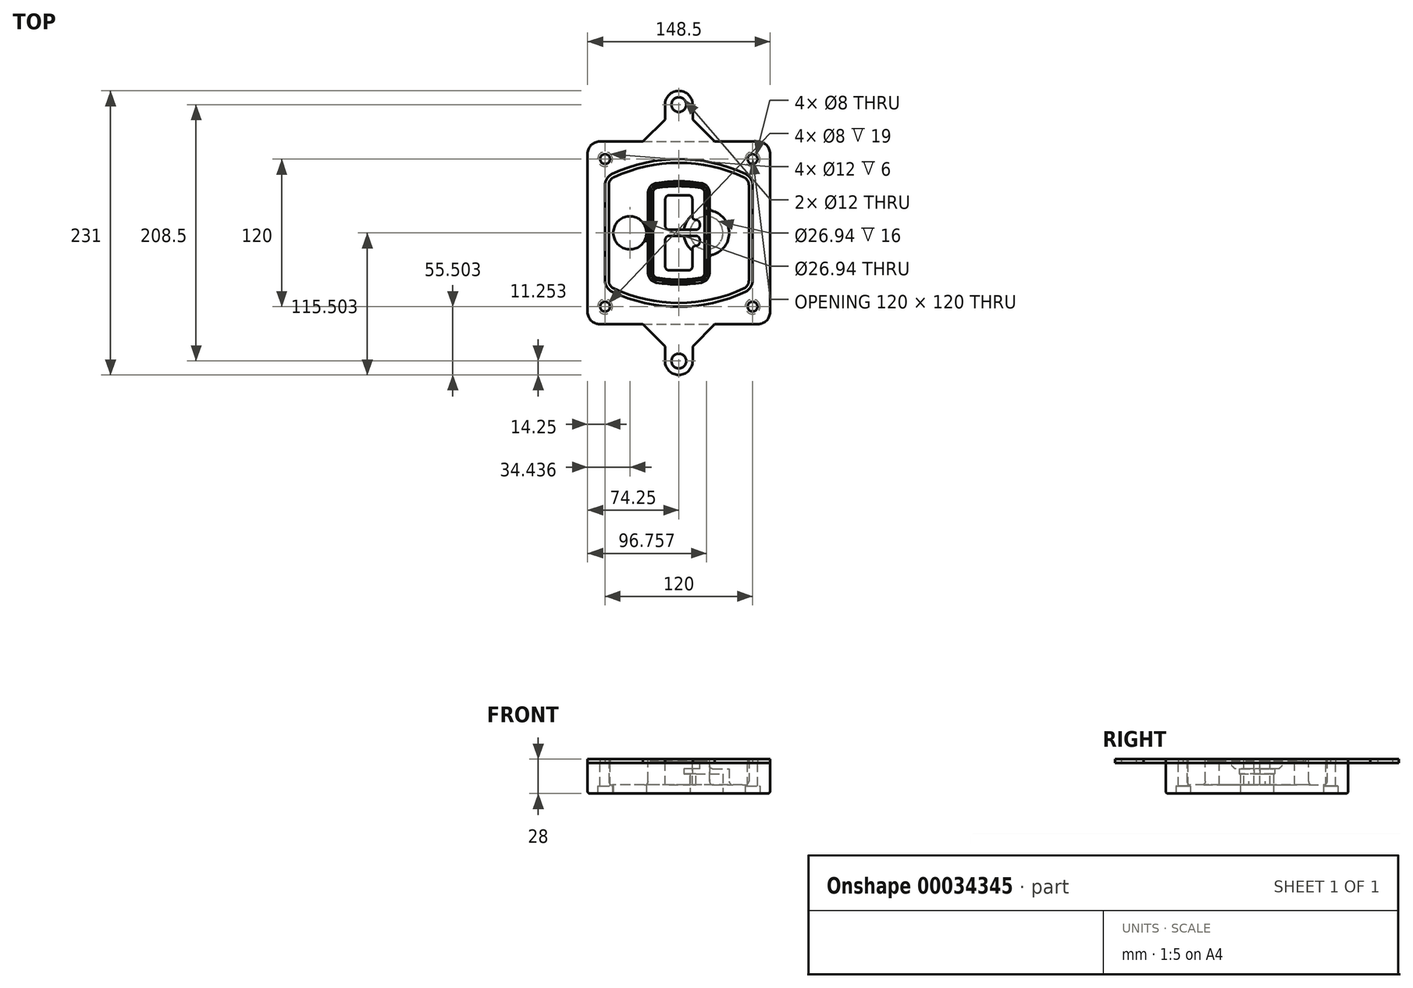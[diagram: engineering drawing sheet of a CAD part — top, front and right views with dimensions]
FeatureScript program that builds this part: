
annotation { "Feature Type Name" : "Feature", "Feature Type Description" : "" }
export const myFeature = defineFeature(function(context is Context, id is Id, definition is map)
    precondition{}
    {
        {
            var Q0;
            {var subQ0=sQuery(id+"F1.wireOp",EDGE,"E1.bottom");var subQ1=sQuery(id+"F1.wireOp",EDGE,"E1.top");var subQ2=sQuery(id+"F1.wireOp",EDGE,"E1.left");var subQ3=sQuery(id+"F1.wireOp",EDGE,"E1.right");var subQ4=sQuery(id+"F1.wireOp",EDGE,"E4");var subQ5=sQuery(id+"F1.wireOp",EDGE,"E5");var subQ6=sQuery(id+"F1.wireOp",EDGE,"E6");var subQ7=sQuery(id+"F1.wireOp",EDGE,"E7");var subQ8=sQuery(id+"F1.wireOp",EDGE,"E21.filletArc");var subQ9=sQuery(id+"F1.wireOp",EDGE,"E22.filletArc");var subQ10=sQuery(id+"F1.wireOp",EDGE,"E23.filletArc");var subQ11=sQuery(id+"F1.wireOp",EDGE,"E24.filletArc");Q0=makeQuery(id+"F3.boolean.opBoolean","SPLIT",FACE,{"disambiguationData":[TD([makeQuery(id+"F2.opExtrude","SWEPT_FACE",FACE,{"disambiguationData":[OSD([subQ0])]})])],"derivedFrom":makeQuery(id+"F2.opExtrude","CAP_FACE",FACE,{"disambiguationData":[OSD([subQ0,subQ1,subQ2,subQ3,subQ4,subQ5,subQ6,subQ7,subQ8,subQ9,subQ10,subQ11])],"isStart":true})});}
            var sketch = newSketch(context, id + "F0", { "sketchPlane" : qUnion([Q0])});
            skSolve(sketch);
        }
        {
            var Q0;
            Q0=qCreatedBy(makeId("Top.planeOp"),FACE);
            var sketch = newSketch(context, id + "F1", { "sketchPlane" : qUnion([Q0])});
            skPoint(sketch, "E0.rect.middle", {"position": v(0, 0) * mm});
            skLineSegment(sketch, "E1.bottom", {"start": v(24.05, 28.38) * mm, "end": v(152.55, 28.38) * mm});
            skLineSegment(sketch, "E1.top", {"start": v(24.05, 176.88) * mm, "end": v(152.55, 176.88) * mm});
            skLineSegment(sketch, "E1.left", {"start": v(14.05, 38.38) * mm, "end": v(14.05, 166.88) * mm});
            skLineSegment(sketch, "E1.right", {"start": v(162.55, 38.38) * mm, "end": v(162.55, 166.88) * mm});
            skLineSegment(sketch, "E2", {"start": v(14.05, 176.88) * mm, "end": v(162.55, 28.38) * mm, "construction": true});
            skLineSegment(sketch, "E3", {"start": v(162.55, 176.88) * mm, "end": v(14.05, 28.38) * mm, "construction": true});
            skCircle(sketch, "E4", {"center": v(28.3, 162.63) * mm, "radius": 4 * mm});
            skCircle(sketch, "E5", {"center": v(148.3, 162.63) * mm, "radius": 4 * mm});
            skCircle(sketch, "E6", {"center": v(148.3, 42.63) * mm, "radius": 4 * mm});
            skCircle(sketch, "E7", {"center": v(28.3, 42.63) * mm, "radius": 4 * mm});
            skLineSegment(sketch, "E8", {"start": v(28.3, 162.63) * mm, "end": v(148.3, 162.63) * mm, "construction": true});
            skLineSegment(sketch, "E9", {"start": v(148.3, 162.63) * mm, "end": v(148.3, 42.63) * mm, "construction": true});
            skLineSegment(sketch, "E10", {"start": v(148.3, 42.63) * mm, "end": v(28.3, 42.63) * mm, "construction": true});
            skLineSegment(sketch, "E11", {"start": v(28.3, 42.63) * mm, "end": v(28.3, 162.63) * mm, "construction": true});
            skLineSegment(sketch, "E12", {"start": v(28.3, 141.46) * mm, "end": v(28.3, 63.8) * mm});
            skLineSegment(sketch, "E13", {"start": v(148.3, 141.46) * mm, "end": v(148.3, 63.8) * mm});
            skArc(sketch, "E14", {"start": v(142.56, 150.51) * mm, "mid": v(88.3, 162.63) * mm, "end": v(34.04, 150.51) * mm});
            skArc(sketch, "E15", {"start": v(34.04, 54.75) * mm, "mid": v(88.3, 42.63) * mm, "end": v(142.56, 54.75) * mm});
            skLineSegment(sketch, "E16", {"start": v(28.3, 102.63) * mm, "end": v(148.3, 102.63) * mm, "construction": true});
            skPoint(sketch, "E17.visualSharp", {"position": v(28.3, 57.63) * mm});
            skArc(sketch, "E17.filletArc", {"start": v(28.3, 63.8) * mm, "mid": v(29.86, 58.44) * mm, "end": v(34.04, 54.75) * mm});
            skPoint(sketch, "E18.visualSharp", {"position": v(28.3, 147.63) * mm});
            skArc(sketch, "E18.filletArc", {"start": v(34.04, 150.51) * mm, "mid": v(29.86, 146.82) * mm, "end": v(28.3, 141.46) * mm});
            skPoint(sketch, "E19.visualSharp", {"position": v(148.3, 147.63) * mm});
            skArc(sketch, "E19.filletArc", {"start": v(148.3, 141.46) * mm, "mid": v(146.74, 146.82) * mm, "end": v(142.56, 150.51) * mm});
            skPoint(sketch, "E20.visualSharp", {"position": v(148.3, 57.63) * mm});
            skArc(sketch, "E20.filletArc", {"start": v(142.56, 54.75) * mm, "mid": v(146.74, 58.44) * mm, "end": v(148.3, 63.8) * mm});
            skPoint(sketch, "E21.visualSharp", {"position": v(14.05, 176.88) * mm});
            skArc(sketch, "E21.filletArc", {"start": v(24.05, 176.88) * mm, "mid": v(16.98, 173.95) * mm, "end": v(14.05, 166.88) * mm});
            skPoint(sketch, "E22.visualSharp", {"position": v(162.55, 176.88) * mm});
            skArc(sketch, "E22.filletArc", {"start": v(162.55, 166.88) * mm, "mid": v(159.62, 173.95) * mm, "end": v(152.55, 176.88) * mm});
            skPoint(sketch, "E23.visualSharp", {"position": v(162.55, 28.38) * mm});
            skArc(sketch, "E23.filletArc", {"start": v(152.55, 28.38) * mm, "mid": v(159.62, 31.31) * mm, "end": v(162.55, 38.38) * mm});
            skPoint(sketch, "E24.visualSharp", {"position": v(14.05, 28.38) * mm});
            skArc(sketch, "E24.filletArc", {"start": v(14.05, 38.38) * mm, "mid": v(16.98, 31.31) * mm, "end": v(24.05, 28.38) * mm});
            skArc(sketch, "E25.0", {"start": v(145.3, 141.46) * mm, "mid": v(144.2, 145.22) * mm, "end": v(141.28, 147.8) * mm});
            skLineSegment(sketch, "E25.1", {"start": v(145.3, 141.46) * mm, "end": v(145.3, 63.8) * mm});
            skArc(sketch, "E25.2", {"start": v(141.28, 57.47) * mm, "mid": v(144.2, 60.05) * mm, "end": v(145.3, 63.8) * mm});
            skArc(sketch, "E25.3", {"start": v(35.32, 57.47) * mm, "mid": v(88.3, 45.63) * mm, "end": v(141.28, 57.47) * mm});
            skArc(sketch, "E25.4", {"start": v(31.3, 63.8) * mm, "mid": v(32.4, 60.05) * mm, "end": v(35.32, 57.47) * mm});
            skArc(sketch, "E25.5", {"start": v(141.28, 147.8) * mm, "mid": v(88.3, 159.63) * mm, "end": v(35.32, 147.8) * mm});
            skLineSegment(sketch, "E25.6", {"start": v(31.3, 141.46) * mm, "end": v(31.3, 63.8) * mm});
            skArc(sketch, "E25.7", {"start": v(35.32, 147.8) * mm, "mid": v(32.4, 145.22) * mm, "end": v(31.3, 141.46) * mm});
            skArc(sketch, "E26.0", {"start": v(32.34, 154.13) * mm, "mid": v(26.48, 148.97) * mm, "end": v(24.3, 141.46) * mm});
            skArc(sketch, "E26.1", {"start": v(144.26, 154.13) * mm, "mid": v(88.3, 166.63) * mm, "end": v(32.34, 154.13) * mm});
            skArc(sketch, "E26.2", {"start": v(152.3, 141.46) * mm, "mid": v(150.12, 148.97) * mm, "end": v(144.26, 154.13) * mm});
            skLineSegment(sketch, "E26.3", {"start": v(152.3, 141.46) * mm, "end": v(152.3, 63.8) * mm});
            skArc(sketch, "E26.4", {"start": v(144.26, 51.13) * mm, "mid": v(150.12, 56.3) * mm, "end": v(152.3, 63.8) * mm});
            skLineSegment(sketch, "E26.5", {"start": v(24.3, 141.46) * mm, "end": v(24.3, 63.8) * mm});
            skArc(sketch, "E26.6", {"start": v(32.34, 51.13) * mm, "mid": v(88.3, 38.63) * mm, "end": v(144.26, 51.13) * mm});
            skArc(sketch, "E26.7", {"start": v(24.3, 63.8) * mm, "mid": v(26.48, 56.3) * mm, "end": v(32.34, 51.13) * mm});
            skSolve(sketch);
        }
        {
            var Q0;
            Q0=makeQuery(id+"F1.imprint","IMPRINT",FACE,{"disambiguationData":[TD([[makeQuery(id+"F1.imprint","IMPRINT",EDGE,{"derivedFrom":sQuery(id+"F1.wireOp",EDGE,"E1.bottom")}),1.0]])]});
            var Q1;
            Q1=makeQuery(id+"F1.imprint","IMPRINT",FACE,{"disambiguationData":[TD([[makeQuery(id+"F1.imprint","IMPRINT",EDGE,{"derivedFrom":sQuery(id+"F1.wireOp",EDGE,"E12")}),1.0]])]});
            var Q2;
            Q2=makeQuery(id+"F1.imprint","IMPRINT",FACE,{"disambiguationData":[TD([[makeQuery(id+"F1.imprint","IMPRINT",EDGE,{"derivedFrom":sQuery(id+"F1.wireOp",EDGE,"E25.0")}),1.0]])]});
            var Q3;
            Q3=makeQuery(id+"F1.imprint","IMPRINT",FACE,{"disambiguationData":[TD([[makeQuery(id+"F1.imprint","IMPRINT",EDGE,{"derivedFrom":sQuery(id+"F1.wireOp",EDGE,"E12")}),-1.0]])]});
            extrude(context, id + "F2", {"entities" : qUnion([Q0, Q1, Q2, Q3]), "oppositeDirection" : true, "depth" : 25 * mm});
        }
        {
            var Q0;
            Q0=makeQuery(id+"F1.imprint","IMPRINT",FACE,{"disambiguationData":[TD([[makeQuery(id+"F1.imprint","IMPRINT",EDGE,{"derivedFrom":sQuery(id+"F1.wireOp",EDGE,"E12")}),1.0]])]});
            extrude(context, id + "F3", {"entities" : qUnion([Q0]), "operationType" : NewBodyOperationType.ADD, "depth" : 3 * mm});
        }
        {
            var Q0;
            Q0=makeQuery(id+"F1.imprint","IMPRINT",FACE,{"disambiguationData":[TD([[makeQuery(id+"F1.imprint","IMPRINT",EDGE,{"derivedFrom":sQuery(id+"F1.wireOp",EDGE,"E25.0")}),1.0]])]});
            extrude(context, id + "F4", {"entities" : qUnion([Q0]), "operationType" : NewBodyOperationType.REMOVE, "oppositeDirection" : true, "depth" : 18 * mm});
        }
        {
            var Q0;
            Q0=makeQuery(id+"F3.opExtrude","CAP_FACE",FACE,{"disambiguationData":[OSD([sQuery(id+"F1.wireOp",EDGE,"E12"),sQuery(id+"F1.wireOp",EDGE,"E13"),sQuery(id+"F1.wireOp",EDGE,"E14"),sQuery(id+"F1.wireOp",EDGE,"E15"),sQuery(id+"F1.wireOp",EDGE,"E17.filletArc"),sQuery(id+"F1.wireOp",EDGE,"E18.filletArc"),sQuery(id+"F1.wireOp",EDGE,"E19.filletArc"),sQuery(id+"F1.wireOp",EDGE,"E20.filletArc"),sQuery(id+"F1.wireOp",EDGE,"E25.0"),sQuery(id+"F1.wireOp",EDGE,"E25.1"),sQuery(id+"F1.wireOp",EDGE,"E25.2"),sQuery(id+"F1.wireOp",EDGE,"E25.3"),sQuery(id+"F1.wireOp",EDGE,"E25.4"),sQuery(id+"F1.wireOp",EDGE,"E25.5"),sQuery(id+"F1.wireOp",EDGE,"E25.6"),sQuery(id+"F1.wireOp",EDGE,"E25.7")])],"isStart":false});
            var sketch = newSketch(context, id + "F5", { "sketchPlane" : qUnion([Q0])});
            skArc(sketch, "E27.0", {"start": v(69.96, 62.18) * mm, "mid": v(88.3, 60.63) * mm, "end": v(106.64, 62.18) * mm});
            skArc(sketch, "E28.0", {"start": v(106.64, 143.09) * mm, "mid": v(88.3, 144.63) * mm, "end": v(69.96, 143.09) * mm});
            skLineSegment(sketch, "E29", {"start": v(63.3, 135.2) * mm, "end": v(63.3, 70.07) * mm});
            skLineSegment(sketch, "E30", {"start": v(113.3, 135.2) * mm, "end": v(113.3, 70.07) * mm});
            skLineSegment(sketch, "E31", {"start": v(63.3, 141.74) * mm, "end": v(113.3, 141.74) * mm, "construction": true});
            skLineSegment(sketch, "E32", {"start": v(63.3, 63.52) * mm, "end": v(113.3, 63.52) * mm, "construction": true});
            skPoint(sketch, "E33.visualSharp", {"position": v(63.3, 141.74) * mm});
            skArc(sketch, "E33.filletArc", {"start": v(69.96, 143.09) * mm, "mid": v(65.19, 140.36) * mm, "end": v(63.3, 135.2) * mm});
            skPoint(sketch, "E34.visualSharp", {"position": v(113.3, 141.74) * mm});
            skArc(sketch, "E34.filletArc", {"start": v(113.3, 135.2) * mm, "mid": v(111.41, 140.36) * mm, "end": v(106.64, 143.09) * mm});
            skPoint(sketch, "E35.visualSharp", {"position": v(113.3, 63.52) * mm});
            skArc(sketch, "E35.filletArc", {"start": v(106.64, 62.18) * mm, "mid": v(111.41, 64.9) * mm, "end": v(113.3, 70.07) * mm});
            skPoint(sketch, "E36.visualSharp", {"position": v(63.3, 63.52) * mm});
            skArc(sketch, "E36.filletArc", {"start": v(63.3, 70.07) * mm, "mid": v(65.19, 64.9) * mm, "end": v(69.96, 62.18) * mm});
            skArc(sketch, "E37.0", {"start": v(141.28, 147.8) * mm, "mid": v(88.3, 159.63) * mm, "end": v(35.32, 147.8) * mm});
            skArc(sketch, "E37.1", {"start": v(35.32, 147.8) * mm, "mid": v(32.4, 145.22) * mm, "end": v(31.3, 141.46) * mm});
            skLineSegment(sketch, "E37.2", {"start": v(31.3, 141.46) * mm, "end": v(31.3, 63.8) * mm});
            skArc(sketch, "E37.3", {"start": v(31.3, 63.8) * mm, "mid": v(32.4, 60.05) * mm, "end": v(35.32, 57.47) * mm});
            skArc(sketch, "E37.4", {"start": v(35.32, 57.47) * mm, "mid": v(88.3, 45.63) * mm, "end": v(141.28, 57.47) * mm});
            skArc(sketch, "E37.5", {"start": v(141.28, 57.47) * mm, "mid": v(144.2, 60.05) * mm, "end": v(145.3, 63.8) * mm});
            skLineSegment(sketch, "E37.6", {"start": v(145.3, 141.46) * mm, "end": v(145.3, 63.8) * mm});
            skArc(sketch, "E37.7", {"start": v(145.3, 141.46) * mm, "mid": v(144.2, 145.22) * mm, "end": v(141.28, 147.8) * mm});
            skLineSegment(sketch, "E38.0", {"start": v(111.3, 135.2) * mm, "end": v(111.3, 70.07) * mm});
            skArc(sketch, "E38.1", {"start": v(106.3, 64.15) * mm, "mid": v(109.88, 66.2) * mm, "end": v(111.3, 70.07) * mm});
            skArc(sketch, "E38.2", {"start": v(70.3, 64.15) * mm, "mid": v(88.3, 62.63) * mm, "end": v(106.3, 64.15) * mm});
            skArc(sketch, "E38.3", {"start": v(65.3, 70.07) * mm, "mid": v(66.72, 66.2) * mm, "end": v(70.3, 64.15) * mm});
            skLineSegment(sketch, "E38.4", {"start": v(65.3, 135.2) * mm, "end": v(65.3, 70.07) * mm});
            skArc(sketch, "E38.5", {"start": v(111.3, 135.2) * mm, "mid": v(109.88, 139.07) * mm, "end": v(106.3, 141.11) * mm});
            skArc(sketch, "E38.6", {"start": v(70.3, 141.11) * mm, "mid": v(66.72, 139.07) * mm, "end": v(65.3, 135.2) * mm});
            skArc(sketch, "E38.7", {"start": v(106.3, 141.11) * mm, "mid": v(88.3, 142.63) * mm, "end": v(70.3, 141.11) * mm});
            skArc(sketch, "E39.0", {"start": v(109.3, 135.2) * mm, "mid": v(108.36, 137.78) * mm, "end": v(105.97, 139.14) * mm});
            skLineSegment(sketch, "E39.1", {"start": v(109.3, 135.2) * mm, "end": v(109.3, 70.07) * mm});
            skArc(sketch, "E39.2", {"start": v(105.97, 66.12) * mm, "mid": v(108.36, 67.49) * mm, "end": v(109.3, 70.07) * mm});
            skArc(sketch, "E39.3", {"start": v(70.63, 66.12) * mm, "mid": v(88.3, 64.63) * mm, "end": v(105.97, 66.12) * mm});
            skArc(sketch, "E39.4", {"start": v(67.3, 70.07) * mm, "mid": v(68.24, 67.49) * mm, "end": v(70.63, 66.12) * mm});
            skArc(sketch, "E39.5", {"start": v(105.97, 139.14) * mm, "mid": v(88.3, 140.63) * mm, "end": v(70.63, 139.14) * mm});
            skLineSegment(sketch, "E39.6", {"start": v(67.3, 135.2) * mm, "end": v(67.3, 70.07) * mm});
            skArc(sketch, "E39.7", {"start": v(70.63, 139.14) * mm, "mid": v(68.24, 137.78) * mm, "end": v(67.3, 135.2) * mm});
            skLineSegment(sketch, "E40", {"start": v(63.3, 102.63) * mm, "end": v(113.3, 102.63) * mm, "construction": true});
            skLineSegment(sketch, "E41", {"start": v(77.3, 108.13) * mm, "end": v(77.3, 130.13) * mm});
            skLineSegment(sketch, "E42", {"start": v(80.3, 133.13) * mm, "end": v(96.3, 133.13) * mm});
            skLineSegment(sketch, "E43", {"start": v(99.3, 130.13) * mm, "end": v(99.3, 116.13) * mm});
            skLineSegment(sketch, "E44", {"start": v(102.3, 113.13) * mm, "end": v(102.3, 113.13) * mm});
            skLineSegment(sketch, "E45", {"start": v(105.3, 110.13) * mm, "end": v(105.3, 108.13) * mm});
            skLineSegment(sketch, "E46", {"start": v(102.3, 105.13) * mm, "end": v(80.3, 105.13) * mm});
            skPoint(sketch, "E47.visualSharp", {"position": v(77.3, 133.13) * mm});
            skArc(sketch, "E47.filletArc", {"start": v(80.3, 133.13) * mm, "mid": v(78.18, 132.25) * mm, "end": v(77.3, 130.13) * mm});
            skPoint(sketch, "E48.visualSharp", {"position": v(99.3, 133.13) * mm});
            skArc(sketch, "E48.filletArc", {"start": v(99.3, 130.13) * mm, "mid": v(98.42, 132.25) * mm, "end": v(96.3, 133.13) * mm});
            skPoint(sketch, "E49.visualSharp", {"position": v(99.3, 113.13) * mm});
            skArc(sketch, "E49.filletArc", {"start": v(99.3, 116.13) * mm, "mid": v(100.18, 114.01) * mm, "end": v(102.3, 113.13) * mm});
            skPoint(sketch, "E50.visualSharp", {"position": v(105.3, 113.13) * mm});
            skArc(sketch, "E50.filletArc", {"start": v(105.3, 110.13) * mm, "mid": v(104.42, 112.25) * mm, "end": v(102.3, 113.13) * mm});
            skPoint(sketch, "E51.visualSharp", {"position": v(105.3, 105.13) * mm});
            skArc(sketch, "E51.filletArc", {"start": v(102.3, 105.13) * mm, "mid": v(104.42, 106.01) * mm, "end": v(105.3, 108.13) * mm});
            skPoint(sketch, "E52.visualSharp", {"position": v(77.3, 105.13) * mm});
            skArc(sketch, "E52.filletArc", {"start": v(77.3, 108.13) * mm, "mid": v(78.18, 106.01) * mm, "end": v(80.3, 105.13) * mm});
            skLineSegment(sketch, "E53.0.MirrorCS", {"start": v(102.3, 100.13) * mm, "end": v(80.3, 100.13) * mm});
            skArc(sketch, "E54.0.MirrorCS", {"start": v(77.3, 97.13) * mm, "mid": v(78.18, 99.25) * mm, "end": v(80.3, 100.13) * mm});
            skLineSegment(sketch, "E55.0.MirrorCS", {"start": v(77.3, 97.13) * mm, "end": v(77.3, 75.13) * mm});
            skArc(sketch, "E56.0.MirrorCS", {"start": v(80.3, 72.13) * mm, "mid": v(78.18, 73.01) * mm, "end": v(77.3, 75.13) * mm});
            skLineSegment(sketch, "E57.0.MirrorCS", {"start": v(80.3, 72.13) * mm, "end": v(96.3, 72.13) * mm});
            skArc(sketch, "E58.0.MirrorCS", {"start": v(99.3, 75.13) * mm, "mid": v(98.42, 73.01) * mm, "end": v(96.3, 72.13) * mm});
            skLineSegment(sketch, "E59.0.MirrorCS", {"start": v(99.3, 75.13) * mm, "end": v(99.3, 89.13) * mm});
            skArc(sketch, "E60.0.MirrorCS", {"start": v(99.3, 89.13) * mm, "mid": v(100.18, 91.25) * mm, "end": v(102.3, 92.13) * mm});
            skArc(sketch, "E61.0.MirrorCS", {"start": v(105.3, 95.13) * mm, "mid": v(104.42, 93.01) * mm, "end": v(102.3, 92.13) * mm});
            skLineSegment(sketch, "E62.0.MirrorCS", {"start": v(105.3, 95.13) * mm, "end": v(105.3, 97.13) * mm});
            skArc(sketch, "E63.0.MirrorCS", {"start": v(102.3, 100.13) * mm, "mid": v(104.42, 99.25) * mm, "end": v(105.3, 97.13) * mm});
            skSolve(sketch);
        }
        {
            var Q0;
            Q0=makeQuery(id+"F5.imprint","IMPRINT",FACE,{"disambiguationData":[TD([[makeQuery(id+"F5.imprint","IMPRINT",EDGE,{"derivedFrom":sQuery(id+"F5.wireOp",EDGE,"E27.0")}),1.0]])]});
            var Q1;
            Q1=makeQuery(id+"F5.imprint","IMPRINT",FACE,{"disambiguationData":[TD([[makeQuery(id+"F5.imprint","IMPRINT",EDGE,{"derivedFrom":sQuery(id+"F5.wireOp",EDGE,"E38.0")}),-1.0]])]});
            var Q2;
            Q2=makeQuery(id+"F5.imprint","IMPRINT",FACE,{"disambiguationData":[TD([[makeQuery(id+"F5.imprint","IMPRINT",EDGE,{"derivedFrom":sQuery(id+"F5.wireOp",EDGE,"E39.0")}),1.0]])]});
            extrude(context, id + "F6", {"entities" : qUnion([Q0, Q1, Q2]), "operationType" : NewBodyOperationType.ADD, "endBound" : BoundingType.UP_TO_NEXT, "oppositeDirection" : true, "depth" : 25 * mm});
        }
        {
            var Q0;
            Q0=makeQuery(id+"F5.imprint","IMPRINT",FACE,{"disambiguationData":[TD([[makeQuery(id+"F5.imprint","IMPRINT",EDGE,{"derivedFrom":sQuery(id+"F5.wireOp",EDGE,"E38.0")}),-1.0]])]});
            extrude(context, id + "F7", {"entities" : qUnion([Q0]), "operationType" : NewBodyOperationType.REMOVE, "oppositeDirection" : true, "depth" : 2 * mm});
        }
        {
            var Q0;
            Q0=makeQuery(id+"F2.opExtrude","CAP_FACE",FACE,{"disambiguationData":[OSD([sQuery(id+"F1.wireOp",EDGE,"E1.bottom"),sQuery(id+"F1.wireOp",EDGE,"E1.top"),sQuery(id+"F1.wireOp",EDGE,"E1.left"),sQuery(id+"F1.wireOp",EDGE,"E1.right"),sQuery(id+"F1.wireOp",EDGE,"E4"),sQuery(id+"F1.wireOp",EDGE,"E5"),sQuery(id+"F1.wireOp",EDGE,"E6"),sQuery(id+"F1.wireOp",EDGE,"E7"),sQuery(id+"F1.wireOp",EDGE,"E21.filletArc"),sQuery(id+"F1.wireOp",EDGE,"E22.filletArc"),sQuery(id+"F1.wireOp",EDGE,"E23.filletArc"),sQuery(id+"F1.wireOp",EDGE,"E24.filletArc")])],"isStart":false});
            var sketch = newSketch(context, id + "F8", { "sketchPlane" : qUnion([Q0])});
            skCircle(sketch, "E64", {"center": v(110.8, -102.63) * mm, "radius": 13.47 * mm});
            skCircle(sketch, "E65", {"center": v(48.49, -102.63) * mm, "radius": 13.47 * mm});
            skLineSegment(sketch, "E66", {"start": v(162.55, -102.63) * mm, "end": v(14.05, -102.63) * mm});
            skCircle(sketch, "E67", {"center": v(110.8, -102.63) * mm, "radius": 18.47 * mm});
            skCircle(sketch, "E68", {"center": v(148.3, -162.63) * mm, "radius": 6 * mm});
            skCircle(sketch, "E69", {"center": v(28.3, -162.63) * mm, "radius": 6 * mm});
            skCircle(sketch, "E70", {"center": v(28.3, -42.63) * mm, "radius": 6 * mm});
            skCircle(sketch, "E71", {"center": v(148.3, -42.63) * mm, "radius": 6 * mm});
            skSolve(sketch);
        }
        {
            var Q0;
            {var subQ1=sQuery(id+"F8.wireOp",EDGE,"E66");var subQ4=sQuery(id+"F8.wireOp",EDGE,"E64");var subQ6=makeQuery(id+"F8.imprint","INTERSECT",VERTEX,{"disambiguationData":[OD(0.0)],"derivedFrom":[subQ4,subQ1]});Q0=makeQuery(id+"F8.imprint","IMPRINT",FACE,{"disambiguationData":[TD([[makeQuery(id+"F8.imprint","IMPRINT",EDGE,{"disambiguationData":[TD([[subQ6,-1.0]])],"derivedFrom":subQ4}),-1.0]])]});}
            var Q1;
            {var subQ0=sQuery(id+"F8.wireOp",EDGE,"E66");var subQ1=sQuery(id+"F8.wireOp",EDGE,"E64");var subQ3=makeQuery(id+"F8.imprint","INTERSECT",VERTEX,{"disambiguationData":[OD(0.0)],"derivedFrom":[subQ1,subQ0]});Q1=makeQuery(id+"F8.imprint","IMPRINT",FACE,{"disambiguationData":[TD([[makeQuery(id+"F8.imprint","IMPRINT",EDGE,{"disambiguationData":[TD([[subQ3,-1.0]])],"derivedFrom":subQ1}),1.0]])]});}
            var Q2;
            {var subQ0=sQuery(id+"F8.wireOp",EDGE,"E66");var subQ1=sQuery(id+"F8.wireOp",EDGE,"E64");var subQ3=makeQuery(id+"F8.imprint","INTERSECT",VERTEX,{"disambiguationData":[OD(0.0)],"derivedFrom":[subQ1,subQ0]});Q2=makeQuery(id+"F8.imprint","IMPRINT",FACE,{"disambiguationData":[TD([[makeQuery(id+"F8.imprint","IMPRINT",EDGE,{"disambiguationData":[TD([[subQ3,1.0]])],"derivedFrom":subQ1}),1.0]])]});}
            var Q3;
            {var subQ1=sQuery(id+"F8.wireOp",EDGE,"E66");var subQ4=sQuery(id+"F8.wireOp",EDGE,"E64");var subQ6=makeQuery(id+"F8.imprint","INTERSECT",VERTEX,{"disambiguationData":[OD(0.0)],"derivedFrom":[subQ4,subQ1]});Q3=makeQuery(id+"F8.imprint","IMPRINT",FACE,{"disambiguationData":[TD([[makeQuery(id+"F8.imprint","IMPRINT",EDGE,{"disambiguationData":[TD([[subQ6,1.0]])],"derivedFrom":subQ4}),-1.0]])]});}
            extrude(context, id + "F9", {"entities" : qUnion([Q0, Q1, Q2, Q3]), "operationType" : NewBodyOperationType.ADD, "oppositeDirection" : true, "depth" : 20 * mm});
        }
        {
            var Q0;
            {var subQ0=sQuery(id+"F8.wireOp",EDGE,"E66");var subQ1=sQuery(id+"F8.wireOp",EDGE,"E64");var subQ3=makeQuery(id+"F8.imprint","INTERSECT",VERTEX,{"disambiguationData":[OD(0.0)],"derivedFrom":[subQ1,subQ0]});Q0=makeQuery(id+"F8.imprint","IMPRINT",FACE,{"disambiguationData":[TD([[makeQuery(id+"F8.imprint","IMPRINT",EDGE,{"disambiguationData":[TD([[subQ3,-1.0]])],"derivedFrom":subQ1}),1.0]])]});}
            var Q1;
            {var subQ0=sQuery(id+"F8.wireOp",EDGE,"E66");var subQ1=sQuery(id+"F8.wireOp",EDGE,"E64");var subQ3=makeQuery(id+"F8.imprint","INTERSECT",VERTEX,{"disambiguationData":[OD(0.0)],"derivedFrom":[subQ1,subQ0]});Q1=makeQuery(id+"F8.imprint","IMPRINT",FACE,{"disambiguationData":[TD([[makeQuery(id+"F8.imprint","IMPRINT",EDGE,{"disambiguationData":[TD([[subQ3,1.0]])],"derivedFrom":subQ1}),1.0]])]});}
            extrude(context, id + "F10", {"entities" : qUnion([Q0, Q1]), "operationType" : NewBodyOperationType.REMOVE, "oppositeDirection" : true, "depth" : 16 * mm});
        }
        {
            var Q0;
            {var subQ0=sQuery(id+"F8.wireOp",EDGE,"E66");var subQ1=sQuery(id+"F8.wireOp",EDGE,"E65");var subQ3=makeQuery(id+"F8.imprint","INTERSECT",VERTEX,{"disambiguationData":[OD(0.0)],"derivedFrom":[subQ1,subQ0]});Q0=makeQuery(id+"F8.imprint","IMPRINT",FACE,{"disambiguationData":[TD([[makeQuery(id+"F8.imprint","IMPRINT",EDGE,{"disambiguationData":[TD([[subQ3,-1.0]])],"derivedFrom":subQ1}),1.0]])]});}
            var Q1;
            {var subQ0=sQuery(id+"F8.wireOp",EDGE,"E66");var subQ1=sQuery(id+"F8.wireOp",EDGE,"E65");var subQ3=makeQuery(id+"F8.imprint","INTERSECT",VERTEX,{"disambiguationData":[OD(0.0)],"derivedFrom":[subQ1,subQ0]});Q1=makeQuery(id+"F8.imprint","IMPRINT",FACE,{"disambiguationData":[TD([[makeQuery(id+"F8.imprint","IMPRINT",EDGE,{"disambiguationData":[TD([[subQ3,1.0]])],"derivedFrom":subQ1}),1.0]])]});}
            extrude(context, id + "F11", {"entities" : qUnion([Q0, Q1]), "operationType" : NewBodyOperationType.REMOVE, "oppositeDirection" : true, "depth" : 25 * mm});
        }
        {
            var Q0;
            Q0=makeQuery(id+"F8.imprint","IMPRINT",FACE,{"disambiguationData":[TD([[makeQuery(id+"F8.imprint","IMPRINT",EDGE,{"derivedFrom":sQuery(id+"F8.wireOp",EDGE,"E68")}),1.0]])]});
            var Q1;
            Q1=makeQuery(id+"F8.imprint","IMPRINT",FACE,{"disambiguationData":[TD([[makeQuery(id+"F8.imprint","IMPRINT",EDGE,{"derivedFrom":makeQuery(id+"F2.opExtrude","CAP_EDGE",EDGE,{"disambiguationData":[OSD([sQuery(id+"F1.wireOp",EDGE,"E5")])],"isStart":false})}),-1.0]])]});
            var Q2;
            Q2=makeQuery(id+"F8.imprint","IMPRINT",FACE,{"disambiguationData":[TD([[makeQuery(id+"F8.imprint","IMPRINT",EDGE,{"derivedFrom":sQuery(id+"F8.wireOp",EDGE,"E69")}),1.0]])]});
            var Q3;
            Q3=makeQuery(id+"F8.imprint","IMPRINT",FACE,{"disambiguationData":[TD([[makeQuery(id+"F8.imprint","IMPRINT",EDGE,{"derivedFrom":makeQuery(id+"F2.opExtrude","CAP_EDGE",EDGE,{"disambiguationData":[OSD([sQuery(id+"F1.wireOp",EDGE,"E4")])],"isStart":false})}),-1.0]])]});
            var Q4;
            Q4=makeQuery(id+"F8.imprint","IMPRINT",FACE,{"disambiguationData":[TD([[makeQuery(id+"F8.imprint","IMPRINT",EDGE,{"derivedFrom":sQuery(id+"F8.wireOp",EDGE,"E70")}),1.0]])]});
            var Q5;
            Q5=makeQuery(id+"F8.imprint","IMPRINT",FACE,{"disambiguationData":[TD([[makeQuery(id+"F8.imprint","IMPRINT",EDGE,{"derivedFrom":makeQuery(id+"F2.opExtrude","CAP_EDGE",EDGE,{"disambiguationData":[OSD([sQuery(id+"F1.wireOp",EDGE,"E7")])],"isStart":false})}),-1.0]])]});
            var Q6;
            Q6=makeQuery(id+"F8.imprint","IMPRINT",FACE,{"disambiguationData":[TD([[makeQuery(id+"F8.imprint","IMPRINT",EDGE,{"derivedFrom":sQuery(id+"F8.wireOp",EDGE,"E71")}),1.0]])]});
            var Q7;
            Q7=makeQuery(id+"F8.imprint","IMPRINT",FACE,{"disambiguationData":[TD([[makeQuery(id+"F8.imprint","IMPRINT",EDGE,{"derivedFrom":makeQuery(id+"F2.opExtrude","CAP_EDGE",EDGE,{"disambiguationData":[OSD([sQuery(id+"F1.wireOp",EDGE,"E6")])],"isStart":false})}),-1.0]])]});
            extrude(context, id + "F12", {"entities" : qUnion([Q0, Q1, Q2, Q3, Q4, Q5, Q6, Q7]), "operationType" : NewBodyOperationType.REMOVE, "oppositeDirection" : true, "depth" : 6 * mm});
        }
        {
            var Q0;
            Q0=makeQuery(id+"F10.boolean.opBoolean","COPY",FACE,{"derivedFrom":makeQuery(id+"F10.opExtrude","CAP_FACE",FACE,{"disambiguationData":[OSD([sQuery(id+"F8.wireOp",EDGE,"E64")])],"isStart":false})});
            var sketch = newSketch(context, id + "F13", { "sketchPlane" : qUnion([Q0])});
            skArc(sketch, "E72.0", {"start": v(99.3, -88.19) * mm, "mid": v(94.75, -93.5) * mm, "end": v(92.5, -100.13) * mm});
            skArc(sketch, "E72.1", {"start": v(92.5, -105.13) * mm, "mid": v(94.75, -111.76) * mm, "end": v(99.3, -117.08) * mm});
            skLineSegment(sketch, "E73", {"start": v(92.5, -105.13) * mm, "end": v(102.3, -105.13) * mm});
            skLineSegment(sketch, "E74.0", {"start": v(102.3, -100.13) * mm, "end": v(92.5, -100.13) * mm});
            skArc(sketch, "E74.1", {"start": v(102.3, -100.13) * mm, "mid": v(104.42, -99.25) * mm, "end": v(105.3, -97.13) * mm});
            skLineSegment(sketch, "E74.2", {"start": v(105.3, -95.13) * mm, "end": v(105.3, -97.13) * mm});
            skArc(sketch, "E74.3", {"start": v(105.3, -95.13) * mm, "mid": v(104.42, -93.01) * mm, "end": v(102.3, -92.13) * mm});
            skArc(sketch, "E74.4", {"start": v(99.3, -89.13) * mm, "mid": v(100.18, -91.25) * mm, "end": v(102.3, -92.13) * mm});
            skLineSegment(sketch, "E74.5", {"start": v(99.3, -88.19) * mm, "end": v(99.3, -89.13) * mm});
            skLineSegment(sketch, "E74.7", {"start": v(102.3, -105.13) * mm, "end": v(92.5, -105.13) * mm});
            skArc(sketch, "E74.8", {"start": v(102.3, -105.13) * mm, "mid": v(104.42, -106.01) * mm, "end": v(105.3, -108.13) * mm});
            skLineSegment(sketch, "E74.9", {"start": v(105.3, -110.13) * mm, "end": v(105.3, -108.13) * mm});
            skArc(sketch, "E74.10", {"start": v(105.3, -110.13) * mm, "mid": v(104.42, -112.25) * mm, "end": v(102.3, -113.13) * mm});
            skArc(sketch, "E74.11", {"start": v(99.3, -116.13) * mm, "mid": v(100.18, -114.01) * mm, "end": v(102.3, -113.13) * mm});
            skLineSegment(sketch, "E74.12", {"start": v(99.3, -117.08) * mm, "end": v(99.3, -116.13) * mm});
            skPoint(sketch, "E75.orphan", {"position": v(99.3, -130.13) * mm});
            skPoint(sketch, "E76.orphan", {"position": v(80.3, -105.13) * mm});
            skPoint(sketch, "E77.orphan", {"position": v(80.3, -100.13) * mm});
            skPoint(sketch, "E78.orphan", {"position": v(99.3, -75.13) * mm});
            skSolve(sketch);
        }
        {
            var Q0;
            {var subQ7=sQuery(id+"F13.wireOp",EDGE,"E72.0");var subQ14=sQuery(id+"F13.wireOp",EDGE,"E72.1");var subQ16=sQuery(id+"F13.wireOp",EDGE,"E74.1");var subQ18=sQuery(id+"F13.wireOp",EDGE,"E74.8");Q0=qUnion([makeQuery(id+"F13.imprint","IMPRINT",FACE,{"disambiguationData":[TD([[makeQuery(id+"F13.imprint","IMPRINT",EDGE,{"derivedFrom":subQ7}),1.0]])]}),makeQuery(id+"F13.imprint","IMPRINT",FACE,{"disambiguationData":[TD([[makeQuery(id+"F13.imprint","IMPRINT",EDGE,{"derivedFrom":subQ14}),1.0]])]}),makeQuery(id+"F13.imprint","IMPRINT",FACE,{"disambiguationData":[TD([[makeQuery(id+"F13.imprint","IMPRINT",EDGE,{"derivedFrom":subQ16}),1.0]])]}),makeQuery(id+"F13.imprint","IMPRINT",FACE,{"disambiguationData":[TD([[makeQuery(id+"F13.imprint","IMPRINT",EDGE,{"derivedFrom":subQ18}),-1.0]])]})]);}
            var Q1;
            Q1=makeQuery(id+"F6.boolean.opBoolean","SPLIT",FACE,{"disambiguationData":[TD([makeQuery(id+"F6.opExtrude","SWEPT_FACE",FACE,{"disambiguationData":[OSD([sQuery(id+"F5.wireOp",EDGE,"E41")])]})])],"derivedFrom":makeQuery(id+"F4.boolean.opBoolean","COPY",FACE,{"derivedFrom":makeQuery(id+"F4.opExtrude","CAP_FACE",FACE,{"disambiguationData":[OSD([sQuery(id+"F1.wireOp",EDGE,"E25.0"),sQuery(id+"F1.wireOp",EDGE,"E25.1"),sQuery(id+"F1.wireOp",EDGE,"E25.2"),sQuery(id+"F1.wireOp",EDGE,"E25.3"),sQuery(id+"F1.wireOp",EDGE,"E25.4"),sQuery(id+"F1.wireOp",EDGE,"E25.5"),sQuery(id+"F1.wireOp",EDGE,"E25.6"),sQuery(id+"F1.wireOp",EDGE,"E25.7")])],"isStart":false})})});
            extrude(context, id + "F14", {"entities" : qUnion([Q0]), "operationType" : NewBodyOperationType.REMOVE, "endBound" : BoundingType.UP_TO_SURFACE, "endBoundEntityFace" : qUnion([Q1]), "depth" : 25 * mm});
        }
        {
            var Q0;
            Q0=makeQuery(id+"F4.boolean.opBoolean","COPY",EDGE,{"derivedFrom":makeQuery(id+"F4.opExtrude","CAP_EDGE",EDGE,{"disambiguationData":[OSD([sQuery(id+"F1.wireOp",EDGE,"E25.6")])],"isStart":false})});
            var Q1;
            Q1=makeQuery(id+"F9.boolean.opBoolean","INTERSECT",EDGE,{"derivedFrom":[makeQuery(id+"F6.opExtrude","SWEPT_FACE",FACE,{"disambiguationData":[OSD([sQuery(id+"F5.wireOp",EDGE,"E30")])]}),makeQuery(id+"F9.opExtrude","CAP_FACE",FACE,{"disambiguationData":[OSD([sQuery(id+"F8.wireOp",EDGE,"E67")])],"isStart":false})]});
            var Q2;
            Q2=makeQuery(id+"F9.boolean.opBoolean","INTERSECT",EDGE,{"disambiguationData":[OD(1.0)],"derivedFrom":[makeQuery(id+"F6.opExtrude","SWEPT_FACE",FACE,{"disambiguationData":[OSD([sQuery(id+"F5.wireOp",EDGE,"E30")])]}),makeQuery(id+"F9.opExtrude","SWEPT_FACE",FACE,{"disambiguationData":[OSD([sQuery(id+"F8.wireOp",EDGE,"E67")])]})]});
            var Q3;
            {var subQ0=sQuery(id+"F5.wireOp",EDGE,"E30");Q3=makeQuery(id+"F9.boolean.opBoolean","SPLIT",EDGE,{"disambiguationData":[TD([makeQuery(id+"F6.opExtrude","SWEPT_FACE",FACE,{"disambiguationData":[OSD([sQuery(id+"F5.wireOp",EDGE,"E35.filletArc")])]})])],"derivedFrom":makeQuery(id+"F6.opExtrude","CAP_EDGE",EDGE,{"disambiguationData":[OSD([subQ0])],"isStart":false})});}
            var Q4;
            {var subQ0=sQuery(id+"F1.wireOp",EDGE,"E25.7");var subQ1=sQuery(id+"F1.wireOp",EDGE,"E25.1");var subQ2=sQuery(id+"F1.wireOp",EDGE,"E25.6");var subQ3=sQuery(id+"F1.wireOp",EDGE,"E25.5");var subQ4=sQuery(id+"F1.wireOp",EDGE,"E25.4");var subQ5=sQuery(id+"F1.wireOp",EDGE,"E25.0");var subQ6=sQuery(id+"F1.wireOp",EDGE,"E25.2");var subQ7=sQuery(id+"F1.wireOp",EDGE,"E25.3");Q4=makeQuery(id+"F9.boolean.opBoolean","INTERSECT",EDGE,{"derivedFrom":[makeQuery(id+"F6.boolean.opBoolean","SPLIT",FACE,{"disambiguationData":[TD([makeQuery(id+"F3.opExtrude","SWEPT_FACE",FACE,{"disambiguationData":[OSD([subQ5])]})])],"derivedFrom":makeQuery(id+"F4.boolean.opBoolean","COPY",FACE,{"derivedFrom":makeQuery(id+"F4.opExtrude","CAP_FACE",FACE,{"disambiguationData":[OSD([subQ5,subQ1,subQ6,subQ7,subQ4,subQ3,subQ2,subQ0])],"isStart":false})})}),makeQuery(id+"F9.opExtrude","SWEPT_FACE",FACE,{"disambiguationData":[OSD([sQuery(id+"F8.wireOp",EDGE,"E67")])]})]});}
            var Q5;
            Q5=makeQuery(id+"F9.boolean.opBoolean","INTERSECT",EDGE,{"disambiguationData":[OD(0.0)],"derivedFrom":[makeQuery(id+"F6.opExtrude","SWEPT_FACE",FACE,{"disambiguationData":[OSD([sQuery(id+"F5.wireOp",EDGE,"E30")])]}),makeQuery(id+"F9.opExtrude","SWEPT_FACE",FACE,{"disambiguationData":[OSD([sQuery(id+"F8.wireOp",EDGE,"E67")])]})]});
            fillet(context, id + "F15", {"entities" : qUnion([Q0, Q1, Q2, Q3, Q4, Q5]), "radius" : 3 * mm, "tangentPropagation" : true, "allowEdgeOverflow" : false});
        }
        {
            var Q0;
            Q0=makeQuery(id+"F2.opExtrude","CAP_EDGE",EDGE,{"disambiguationData":[OSD([sQuery(id+"F1.wireOp",EDGE,"E1.bottom")])],"isStart":false});
            fillet(context, id + "F16", {"entities" : qUnion([Q0]), "radius" : 2 * mm, "tangentPropagation" : true, "allowEdgeOverflow" : false});
        }
        {
            var Q0;
            {var subQ0=sQuery(id+"F1.wireOp",EDGE,"E22.filletArc");var subQ1=sQuery(id+"F1.wireOp",EDGE,"E7");var subQ2=sQuery(id+"F1.wireOp",EDGE,"E6");var subQ3=sQuery(id+"F1.wireOp",EDGE,"E5");var subQ4=sQuery(id+"F1.wireOp",EDGE,"E4");var subQ5=sQuery(id+"F1.wireOp",EDGE,"E1.bottom");var subQ6=sQuery(id+"F1.wireOp",EDGE,"E21.filletArc");var subQ7=sQuery(id+"F1.wireOp",EDGE,"E1.top");var subQ8=sQuery(id+"F1.wireOp",EDGE,"E1.left");var subQ9=sQuery(id+"F1.wireOp",EDGE,"E1.right");var subQ10=sQuery(id+"F1.wireOp",EDGE,"E23.filletArc");var subQ11=sQuery(id+"F1.wireOp",EDGE,"E24.filletArc");Q0=makeQuery(id+"F3.boolean.opBoolean","SPLIT",FACE,{"disambiguationData":[TD([makeQuery(id+"F2.opExtrude","SWEPT_FACE",FACE,{"disambiguationData":[OSD([subQ5])]})])],"derivedFrom":makeQuery(id+"F2.opExtrude","CAP_FACE",FACE,{"disambiguationData":[OSD([subQ5,subQ7,subQ8,subQ9,subQ4,subQ3,subQ2,subQ1,subQ6,subQ0,subQ10,subQ11])],"isStart":true})});}
            var sketch = newSketch(context, id + "F17", { "sketchPlane" : qUnion([Q0])});
            skPoint(sketch, "E79", {"position": v(59.05, 176.88) * mm});
            skPoint(sketch, "E80", {"position": v(117.55, 176.88) * mm});
            skLineSegment(sketch, "E81", {"start": v(117.55, 176.88) * mm, "end": v(99.55, 194.88) * mm});
            skLineSegment(sketch, "E82", {"start": v(59.05, 176.88) * mm, "end": v(77.05, 194.88) * mm});
            skLineSegment(sketch, "E83", {"start": v(88.3, 176.88) * mm, "end": v(88.3, 206.88) * mm, "construction": true});
            skLineSegment(sketch, "E84", {"start": v(77.05, 194.88) * mm, "end": v(77.05, 206.88) * mm});
            skLineSegment(sketch, "E85", {"start": v(99.55, 194.88) * mm, "end": v(99.55, 206.88) * mm});
            skArc(sketch, "E86", {"start": v(99.55, 206.88) * mm, "mid": v(88.3, 218.13) * mm, "end": v(77.05, 206.88) * mm});
            skCircle(sketch, "E87", {"center": v(88.3, 206.88) * mm, "radius": 6 * mm});
            skLineSegment(sketch, "E88", {"start": v(162.55, 102.63) * mm, "end": v(14.05, 102.63) * mm, "construction": true});
            skLineSegment(sketch, "E89.MirrorCS", {"start": v(117.55, 28.38) * mm, "end": v(99.55, 10.38) * mm});
            skLineSegment(sketch, "E90.MirrorCS", {"start": v(99.55, 10.38) * mm, "end": v(99.55, -1.62) * mm});
            skArc(sketch, "E91.MirrorCS", {"start": v(99.55, -1.62) * mm, "mid": v(88.3, -12.87) * mm, "end": v(77.05, -1.62) * mm});
            skLineSegment(sketch, "E92.MirrorCS", {"start": v(59.05, 28.38) * mm, "end": v(77.05, 10.38) * mm});
            skLineSegment(sketch, "E93.MirrorCS", {"start": v(77.05, 10.38) * mm, "end": v(77.05, -1.62) * mm});
            skCircle(sketch, "E94.MirrorC", {"center": v(88.3, -1.62) * mm, "radius": 6 * mm});
            skSolve(sketch);
        }
        {
            var Q0;
            {var subQ1=sQuery(id+"F17.wireOp",EDGE,"E81");Q0=makeQuery(id+"F17.imprint","IMPRINT",FACE,{"disambiguationData":[TD([[makeQuery(id+"F17.imprint","IMPRINT",EDGE,{"derivedFrom":subQ1}),1.0]])]});}
            var Q1;
            {var subQ0=sQuery(id+"F17.wireOp",EDGE,"E92.MirrorCS");Q1=makeQuery(id+"F17.imprint","IMPRINT",FACE,{"disambiguationData":[TD([[makeQuery(id+"F17.imprint","IMPRINT",EDGE,{"derivedFrom":subQ0}),1.0]])]});}
            var Q2;
            Q2=makeQuery(id+"F17.imprint","IMPRINT",FACE,{"disambiguationData":[TD([[makeQuery(id+"F17.imprint","IMPRINT",EDGE,{"derivedFrom":makeQuery(id+"F2.opExtrude","CAP_EDGE",EDGE,{"disambiguationData":[OSD([sQuery(id+"F1.wireOp",EDGE,"E1.left")])],"isStart":true})}),-1.0]])]});
            extrude(context, id + "F18", {"entities" : qUnion([Q0, Q1, Q2]), "depth" : 3 * mm});
        }
    });
